# Revit family: Hager-FW-Flush_mounted-IP30-With_Cover-With_DIN-Hosted-PL-pl
name_source: partatom
category: Electrical Equipment
units: mm (PartAtom-declared; Revit-internal decimal feet)

## family parameters
Cut with Voids When Loaded = No
Host = Face
Maintain Annotation Orientation = Yes
Panel Configuration = Two Columns, Circuits Across
Part Type = Panelboard
Room Calculation Point = No
Round Connector Dimension = Use Diameter
Shared = No

## types (12) — shared parameters
BC_MODEL_ID = 1554247
BC_OBJECT_ID = 513841
BC_OBJECT_VERSION = #5
Code hager = ADD-EC000214_EU
EF000003 - Sposób montażu = Montaż podtynkowy
EF000007 - Kolor = Biały
EF000024 - Odporność na promieniowanie UV = No
EF000049 - Głębokość = 121 mm  [stored 0.396982 ft]
EF000116 - Numer RAL = 9010
EF000118 - Z płytą montażową = No
EF000218 - Głębokość wbudowania = 110 mm  [stored 0.360892 ft]
EF001062 - Wykonanie zgodne z Dyrektywą Kompatybilności Elektromagnetycznej EMC = No
EF001088 - Możliwość rozbudowy = Yes
EF001134 - Szyna DIN = Yes
EF004462 - Rodzaj zamknięcia = Inne
EF005474 - Stopień ochrony (IP) = IP30
EF006244 - Transparentna pokrywa/drzwi = No
EF006306 - Z zamkiem = No
EF009212 - Wykonanie/rodzaj pokrywy = Zamknięty
EF015776 - Listwa zaciskowa uziemienia = Yes
EF015777 - Listwa zaciskowa przewodu neutralnego = No
EF015941 - Drzwi przepuszczające sygnał = No
ETIM class code = EC000214
ETIM class name = Small distribution board
HG000001-Number of columns-pl = 1
HG000002-with door or cover-pl = Yes
HG000003-Range-pl = FW
HG000005-Thickness-pl = 2 mm  [stored 0.00656168 ft]
HG000006-Flush mounted-pl = Yes
HG000009-Double swing door-pl = No
HG000010-Asymmetric doors-pl = No
HG000011-Empty rows from bottom-pl = No
HG000012-Door swing angle-pl = 90.00°
HG000013-Door on the left-pl = No
HG000014-Door on the right-pl = Yes
HG000015-Clearance visibility-pl = Yes
HG000016-Door 3D visibility-pl = Yes
HG000017-Distance between poles-pl = 18 mm  [stored 0.0590551 ft]
HG000060-RAL-number = 9010
HG000099-Onfly Template ID-pl-PL = 507532
Manufacturer = Hager
Name = FW-Flush_mounted-IP30-With_Cover-With_DIN-PL
Name BIM&CO = Electricity
Name hager = ADD_Enclosures_EC000214
Uniformat = Low Tension Service & Dist.
Uniformat code = D501001
zero-valued in all types: Default Elevation, EF001131 - Głębokość wewnętrzna, HG000007-Number of empty columns-pl, HG000008-Number of empty rows-pl

## per-type parameters (varying)
| type | BC_VARIANT_ID | EF000008 - Szerokość | EF000040 - Wysokość | EF000266 - Liczba rzędów | EF000332 - Wysokość wbudowania | EF000846 - Szerokość wbudowania | EF002950 - Szerokość wyrażona liczbą modułów | HG000004-Manufacturer reference-pl | HGEF000266-Liczba rzędów | HGEF0002950-Szerokość wyrażona liczbą modułów |
| FW-Flush_mounted_W406_H692_D121_12_Modular_Spacing-FW312FT | 1178636 | 406 mm  [stored 1.33202 ft] | 692 mm  [stored 2.27034 ft] | 3 | 692 mm  [stored 2.27034 ft] | 406 mm  [stored 1.33202 ft] | 12 | FW312FT | 3 | 12 |
| FW-Flush_mounted_W622_H692_D121_24_Modular_Spacing-FW324FT | 1178637 | 622 mm  [stored 2.04068 ft] | 692 mm  [stored 2.27034 ft] | 3 | 692 mm  [stored 2.27034 ft] | 622 mm  [stored 2.04068 ft] | 24 | FW324FT | 3 | 24 |
| FW-Flush_mounted_W406_H842_D121_12_Modular_Spacing-FW412FT | 1178638 | 406 mm  [stored 1.33202 ft] | 842 mm  [stored 2.76247 ft] | 4 | 842 mm  [stored 2.76247 ft] | 406 mm  [stored 1.33202 ft] | 12 | FW412FT | 4 | 12 |
| FW-Flush_mounted_W622_H842_D121_24_Modular_Spacing-FW424FT | 1178639 | 622 mm  [stored 2.04068 ft] | 842 mm  [stored 2.76247 ft] | 4 | 842 mm  [stored 2.76247 ft] | 622 mm  [stored 2.04068 ft] | 24 | FW424FT | 4 | 24 |
| FW-Flush_mounted_W838_H842_D121_36_Modular_Spacing-FW436FT | 1178640 | 838 mm  [stored 2.74934 ft] | 842 mm  [stored 2.76247 ft] | 4 | 842 mm  [stored 2.76247 ft] | 838 mm  [stored 2.74934 ft] | 36 | FW436FT | 4 | 36 |
| FW-Flush_mounted_W406_H992_D121_12_Modular_Spacing-FW512FT | 1178641 | 406 mm  [stored 1.33202 ft] | 992 mm  [stored 3.25459 ft] | 5 | 992 mm  [stored 3.25459 ft] | 406 mm  [stored 1.33202 ft] | 12 | FW512FT | 5 | 12 |
| FW-Flush_mounted_W622_H992_D121_24_Modular_Spacing-FW524FT | 1178642 | 622 mm  [stored 2.04068 ft] | 992 mm  [stored 3.25459 ft] | 5 | 992 mm  [stored 3.25459 ft] | 622 mm  [stored 2.04068 ft] | 24 | FW524FT | 5 | 24 |
| FW-Flush_mounted_W838_H992_D121_36_Modular_Spacing-FW536FT | 1178643 | 838 mm  [stored 2.74934 ft] | 992 mm  [stored 3.25459 ft] | 5 | 992 mm  [stored 3.25459 ft] | 838 mm  [stored 2.74934 ft] | 36 | FW536FT | 5 | 36 |
| FW-Flush_mounted_W406_H1142_D121_12_Modular_Spacing-FW612FT | 1178644 | 406 mm  [stored 1.33202 ft] | 1142 mm  [stored 3.74672 ft] | 6 | 1142 mm  [stored 3.74672 ft] | 406 mm  [stored 1.33202 ft] | 12 | FW612FT | 6 | 12 |
| FW-Flush_mounted_W622_H1142_D121_24_Modular_Spacing-FW624FT | 1178645 | 622 mm  [stored 2.04068 ft] | 1142 mm  [stored 3.74672 ft] | 6 | 1142 mm  [stored 3.74672 ft] | 622 mm  [stored 2.04068 ft] | 24 | FW624FT | 6 | 24 |
| FW-Flush_mounted_W838_H1142_D121_36_Modular_Spacing-FW636FT | 1178646 | 838 mm  [stored 2.74934 ft] | 1142 mm  [stored 3.74672 ft] | 6 | 1142 mm  [stored 3.74672 ft] | 838 mm  [stored 2.74934 ft] | 36 | FW636FT | 6 | 36 |
| FW-Flush_mounted_W838_H1292_D121_36_Modular_Spacing-FW736FT | 1178647 | 838 mm  [stored 2.74934 ft] | 1292 mm  [stored 4.23885 ft] | 7 | 1292 mm  [stored 4.23885 ft] | 838 mm  [stored 2.74934 ft] | 36 | FW736FT | 7 | 36 |

note: column(s) folded — value = type name in every type: Reference

note: [stored X ft] marks values corroborated as IEEE doubles in the binary element streams (Revit-internal decimal feet)

## geometry (parser evidence)
native form markers: Sweep x16
no freeform markers — native parametric forms only
